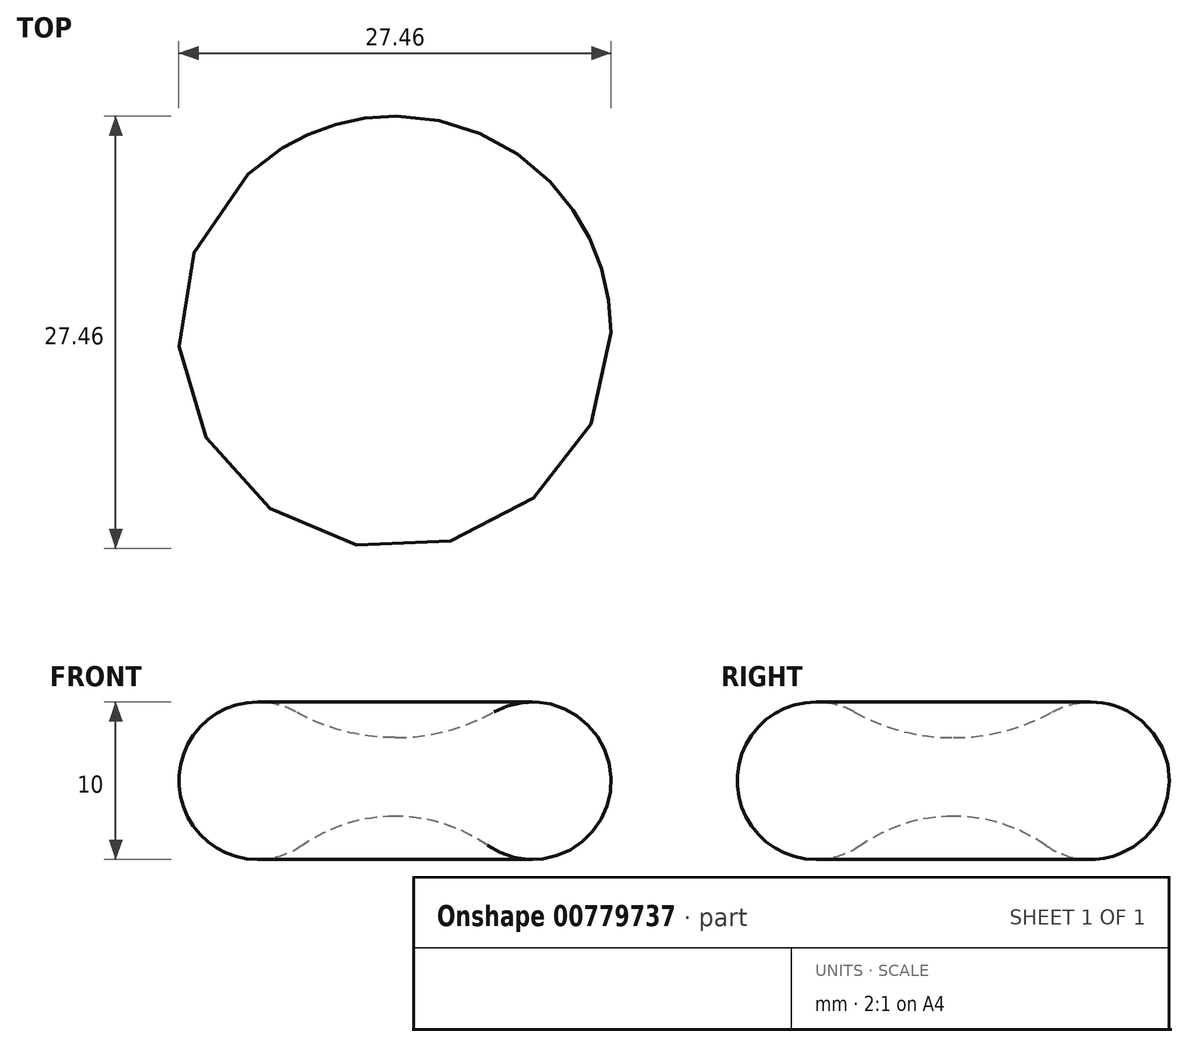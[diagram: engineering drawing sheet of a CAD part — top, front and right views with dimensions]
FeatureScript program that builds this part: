
annotation { "Feature Type Name" : "Feature", "Feature Type Description" : "" }
export const myFeature = defineFeature(function(context is Context, id is Id, definition is map)
    precondition{}
    {
        {
            var Q0;
            Q0=qCreatedBy(makeId("Front.planeOp"),FACE);
            var sketch = newSketch(context, id + "F0", { "sketchPlane" : qUnion([Q0])});
            skArc(sketch, "E0", {"start": v(0, 10.28) * mm, "mid": v(-3.08, 9.81) * mm, "end": v(-5.87, 8.44) * mm});
            skArc(sketch, "E1", {"start": v(-6.3, 16.92) * mm, "mid": v(-3.25, 15.7) * mm, "end": v(0, 15.28) * mm});
            skArc(sketch, "E2", {"start": v(-6.3, 16.92) * mm, "mid": v(-13.72, 12.3) * mm, "end": v(-5.87, 8.44) * mm});
            skLineSegment(sketch, "E3", {"start": v(0, 15.28) * mm, "end": v(0, 10.28) * mm});
            skSolve(sketch);
        }
        {
            var Q0;
            Q0=makeQuery(id+"F0.imprint","IMPRINT",FACE,{"disambiguationData":[TD([[makeQuery(id+"F0.imprint","IMPRINT",EDGE,{"derivedFrom":sQuery(id+"F0.wireOp",EDGE,"E0")}),-1.0]])]});
            var Q1;
            Q1=sQuery(id+"F0.wireOp",EDGE,"E3");
            revolve(context, id + "F1", {"surfaceOperationType" : NewSurfaceOperationType.NEW, "entities" : qUnion([Q0]), "axis" : qUnion([Q1]), "revolveType" : RevolveType.FULL});
        }
    });
